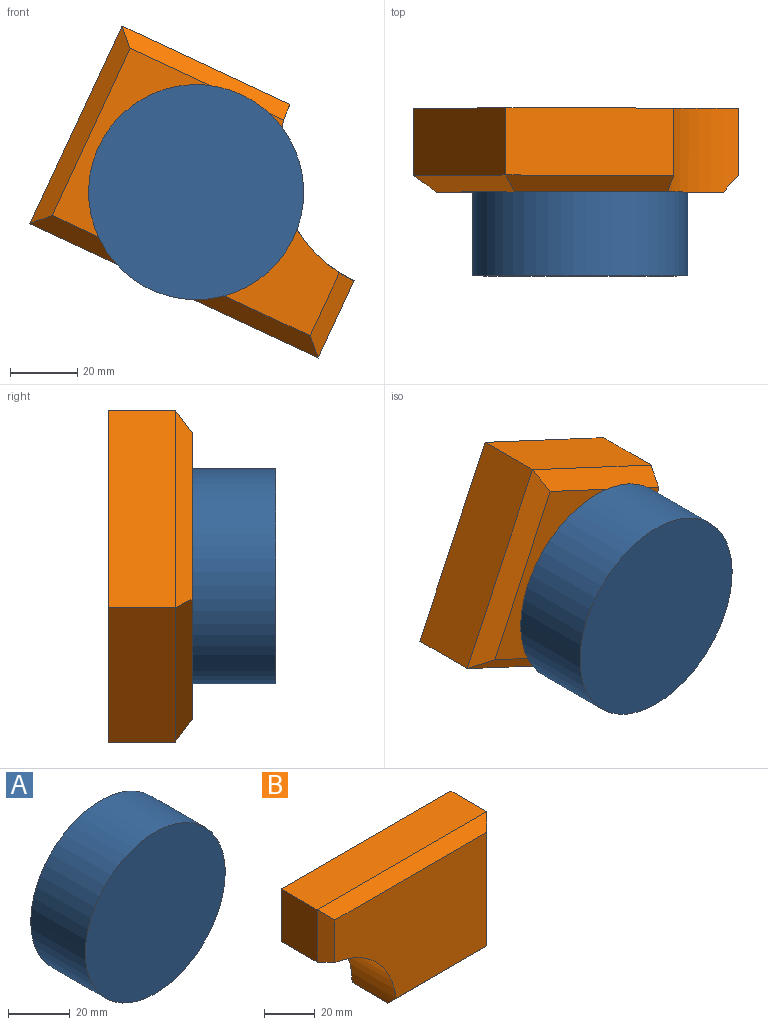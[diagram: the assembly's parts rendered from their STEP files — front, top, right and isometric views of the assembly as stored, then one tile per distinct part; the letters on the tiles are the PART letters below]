
ASSEMBLY  parts=2 mates=1
PART A: 3 faces, bbox 64.1x25x64.1 mm
  f0: cylinder r=32.06mm len=64.11mm, axis (0,1,0), area 5035.3mm2, adj f1,f2
  f1: plane 64.11x64.11mm, normal (0,-1,0), area 3228.2mm2, adj f0
  f2: plane 64.11x64.11mm, normal (0,1,0), area 3228.2mm2, adj f0
PART B: 11 faces, bbox 94.8x25x65 mm
  f0: plane 94.84x64.97mm, normal (0,1,0), area 4929.9mm2, adj f1,f2,f3,f4,f10
  f1: plane 94.84x20mm, normal (0,0,1), area 1896.8mm2, adj f0,f2,f4,f7
  f2: plane 25.37x20mm, normal (-1,0,0), area 507.3mm2, adj f0,f1,f6,f10
  f3: plane 55.23x20mm, normal (0,0,-1), area 1104.6mm2, adj f0,f4,f8,f10
  f4: plane 64.97x20mm, normal (1,0,0), area 1299.5mm2, adj f0,f1,f3,f9
  f5: plane 84.84x54.97mm, normal (0,-1,0), area 3801.8mm2, adj f6,f7,f8,f9,f10
  f6: plane 25.69x5.01mm, normal (-0.71,-0.71,0), area 162.4mm2, adj f2,f5,f7,f10
  f7: plane 94.84x5mm, normal (0,-0.71,0.71), area 635.3mm2, adj f1,f5,f6,f9
  f8: plane 55.56x5.01mm, normal (0,-0.71,-0.71), area 373.6mm2, adj f3,f5,f9,f10
  f9: plane 64.97x5mm, normal (0.71,-0.71,0), area 424.1mm2, adj f4,f5,f7,f8
  f10: cylinder r=39.61mm len=39.61mm, axis (0,1,0), area 1530.3mm2, adj f0,f2,f3,f5,f6,f8
PLACE A rot(axis=(0,-1,0),155deg) t=(-32.43,-22.39,71.33)mm
PLACE B rot(axis=(0,-1,0),155deg) t=(-14.19,2.61,71.65)mm
MATE fastened B.f5 <-> A.f0  axis (0,-1,0) through (-41.41,-22.39,52.07)mm
